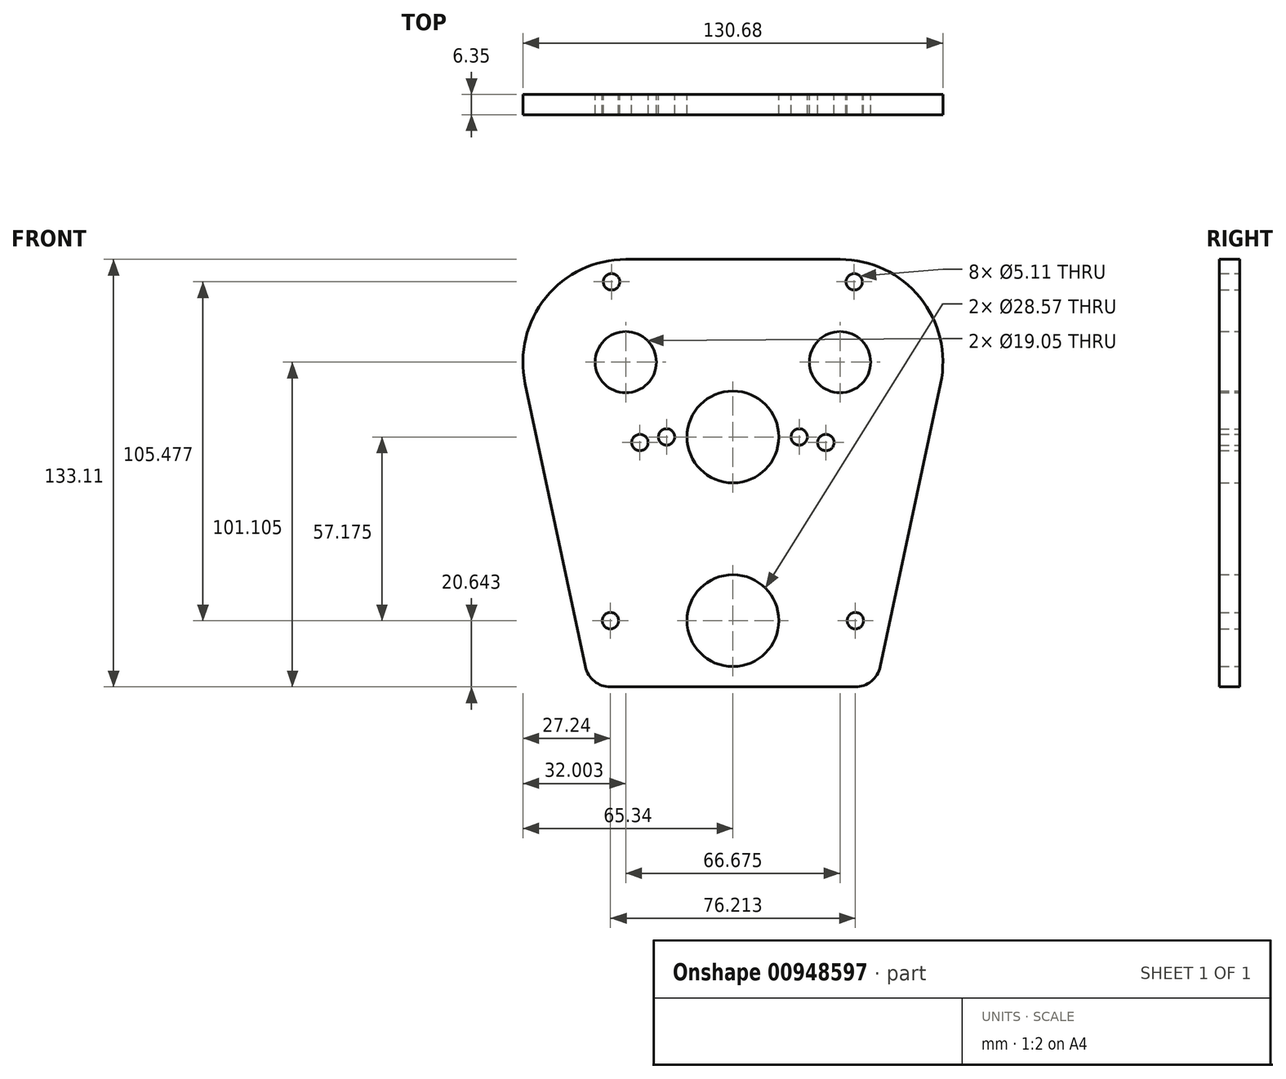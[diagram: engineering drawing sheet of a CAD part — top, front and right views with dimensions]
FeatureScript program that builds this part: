
annotation { "Feature Type Name" : "Feature", "Feature Type Description" : "" }
export const myFeature = defineFeature(function(context is Context, id is Id, definition is map)
    precondition{}
    {
        {
            var Q0;
            Q0=qCreatedBy(makeId("Front.planeOp"),FACE);
            var sketch = newSketch(context, id + "F0", { "sketchPlane" : qUnion([Q0])});
            skLineSegment(sketch, "E0.bottom", {"start": v(304.8, 23.81) * mm, "end": v(-304.8, 23.81) * mm, "construction": true});
            skLineSegment(sketch, "E0.top", {"start": v(304.8, -26.99) * mm, "end": v(-304.8, -26.99) * mm, "construction": true});
            skLineSegment(sketch, "E0.left", {"start": v(304.8, 23.81) * mm, "end": v(304.8, -26.99) * mm, "construction": true});
            skLineSegment(sketch, "E0.right", {"start": v(-304.8, 23.81) * mm, "end": v(-304.8, -26.99) * mm, "construction": true});
            skPoint(sketch, "E0.middle", {"position": v(0, -1.59) * mm});
            skCircle(sketch, "E1", {"center": v(-33.34, 78.87) * mm, "radius": 32 * mm, "construction": true});
            skCircle(sketch, "E2", {"center": v(33.34, 78.87) * mm, "radius": 32 * mm, "construction": true});
            skCircle(sketch, "E3", {"center": v(33.34, 78.87) * mm, "radius": 8.9 * mm, "construction": true});
            skCircle(sketch, "E4", {"center": v(-33.34, 78.87) * mm, "radius": 8.9 * mm, "construction": true});
            skLineSegment(sketch, "E5", {"start": v(0, -1.59) * mm, "end": v(0, 78.87) * mm, "construction": true});
            skLineSegment(sketch, "E6", {"start": v(-33.34, 78.87) * mm, "end": v(0, 78.87) * mm, "construction": true});
            skLineSegment(sketch, "E7", {"start": v(0, 78.87) * mm, "end": v(33.34, 78.87) * mm, "construction": true});
            skCircle(sketch, "E8", {"center": v(0, 55.59) * mm, "radius": 31.76 * mm, "construction": true});
            skCircle(sketch, "E9", {"center": v(0, 55.59) * mm, "radius": 19.06 * mm, "construction": true});
            skCircle(sketch, "E10", {"center": v(0, -1.59) * mm, "radius": 38.11 * mm, "construction": true});
            skCircle(sketch, "E11", {"center": v(0, -1.59) * mm, "radius": 50.8 * mm, "construction": true});
            skCircle(sketch, "E12", {"center": v(0, -1.59) * mm, "radius": 25.41 * mm, "construction": true});
            skCircle(sketch, "E13", {"center": v(-33.34, 78.87) * mm, "radius": 9.53 * mm});
            skCircle(sketch, "E14", {"center": v(33.34, 78.87) * mm, "radius": 9.53 * mm});
            skCircle(sketch, "E15", {"center": v(0, 55.59) * mm, "radius": 14.29 * mm});
            skCircle(sketch, "E16", {"center": v(0, -1.59) * mm, "radius": 14.29 * mm});
            skLineSegment(sketch, "E17", {"start": v(-28.93, 53.86) * mm, "end": v(-33.34, 78.87) * mm, "construction": true});
            skLineSegment(sketch, "E18", {"start": v(-33.34, 78.87) * mm, "end": v(-37.75, 103.89) * mm, "construction": true});
            skCircle(sketch, "E19", {"center": v(-28.93, 53.86) * mm, "radius": 2.55 * mm});
            skCircle(sketch, "E20", {"center": v(-37.75, 103.89) * mm, "radius": 2.55 * mm});
            skCircle(sketch, "E21.MirrorC", {"center": v(37.75, 103.89) * mm, "radius": 2.55 * mm});
            skLineSegment(sketch, "E22.MirrorCS", {"start": v(33.34, 78.87) * mm, "end": v(37.75, 103.89) * mm, "construction": true});
            skCircle(sketch, "E23.MirrorC", {"center": v(28.93, 53.86) * mm, "radius": 2.55 * mm});
            skLineSegment(sketch, "E24.MirrorCS", {"start": v(28.93, 53.86) * mm, "end": v(33.34, 78.87) * mm, "construction": true});
            skArc(sketch, "E25", {"start": v(-33.34, 110.88) * mm, "mid": v(-58.21, 99.01) * mm, "end": v(-64.64, 72.2) * mm});
            skCircle(sketch, "E26", {"center": v(-292.1, 11.11) * mm, "radius": 2.55 * mm, "construction": true});
            skCircle(sketch, "E27.0.1.0", {"center": v(-292.1, -14.29) * mm, "radius": 2.55 * mm, "construction": true});
            skCircle(sketch, "E27.1.0.0", {"center": v(-266.7, 11.11) * mm, "radius": 2.55 * mm, "construction": true});
            skCircle(sketch, "E27.1.1.0", {"center": v(-266.7, -14.29) * mm, "radius": 2.55 * mm, "construction": true});
            skCircle(sketch, "E27.2.0.0", {"center": v(-241.3, 11.11) * mm, "radius": 2.55 * mm, "construction": true});
            skCircle(sketch, "E27.2.1.0", {"center": v(-241.3, -14.29) * mm, "radius": 2.55 * mm, "construction": true});
            skCircle(sketch, "E27.3.0.0", {"center": v(-215.9, 11.11) * mm, "radius": 2.55 * mm, "construction": true});
            skCircle(sketch, "E27.3.1.0", {"center": v(-215.9, -14.29) * mm, "radius": 2.55 * mm, "construction": true});
            skCircle(sketch, "E27.4.0.0", {"center": v(-190.5, 11.11) * mm, "radius": 2.55 * mm, "construction": true});
            skCircle(sketch, "E27.4.1.0", {"center": v(-190.5, -14.29) * mm, "radius": 2.55 * mm, "construction": true});
            skCircle(sketch, "E27.5.0.0", {"center": v(-165.1, 11.11) * mm, "radius": 2.55 * mm, "construction": true});
            skCircle(sketch, "E27.5.1.0", {"center": v(-165.1, -14.29) * mm, "radius": 2.55 * mm, "construction": true});
            skCircle(sketch, "E27.6.0.0", {"center": v(-139.7, 11.11) * mm, "radius": 2.55 * mm, "construction": true});
            skCircle(sketch, "E27.6.1.0", {"center": v(-139.7, -14.29) * mm, "radius": 2.55 * mm, "construction": true});
            skCircle(sketch, "E27.7.0.0", {"center": v(-114.3, 11.11) * mm, "radius": 2.55 * mm, "construction": true});
            skCircle(sketch, "E27.7.1.0", {"center": v(-114.3, -14.29) * mm, "radius": 2.55 * mm, "construction": true});
            skCircle(sketch, "E27.8.0.0", {"center": v(-88.9, 11.11) * mm, "radius": 2.55 * mm, "construction": true});
            skCircle(sketch, "E27.8.1.0", {"center": v(-88.9, -14.29) * mm, "radius": 2.55 * mm, "construction": true});
            skCircle(sketch, "E27.9.0.0", {"center": v(-63.5, 11.11) * mm, "radius": 2.55 * mm, "construction": true});
            skCircle(sketch, "E27.9.1.0", {"center": v(-63.5, -14.29) * mm, "radius": 2.55 * mm, "construction": true});
            skCircle(sketch, "E27.10.0.0", {"center": v(-38.1, 11.11) * mm, "radius": 2.55 * mm, "construction": true});
            skCircle(sketch, "E27.10.1.0", {"center": v(-38.1, -14.29) * mm, "radius": 2.55 * mm, "construction": true});
            skCircle(sketch, "E27.11.0.0", {"center": v(-12.7, 11.11) * mm, "radius": 2.55 * mm, "construction": true});
            skCircle(sketch, "E27.11.1.0", {"center": v(-12.7, -14.29) * mm, "radius": 2.55 * mm, "construction": true});
            skCircle(sketch, "E27.12.0.0", {"center": v(12.7, 11.11) * mm, "radius": 2.55 * mm, "construction": true});
            skCircle(sketch, "E27.12.1.0", {"center": v(12.7, -14.29) * mm, "radius": 2.55 * mm, "construction": true});
            skCircle(sketch, "E27.13.0.0", {"center": v(38.1, 11.11) * mm, "radius": 2.55 * mm, "construction": true});
            skCircle(sketch, "E27.13.1.0", {"center": v(38.1, -14.29) * mm, "radius": 2.55 * mm, "construction": true});
            skCircle(sketch, "E27.14.0.0", {"center": v(63.5, 11.11) * mm, "radius": 2.55 * mm, "construction": true});
            skCircle(sketch, "E27.14.1.0", {"center": v(63.5, -14.29) * mm, "radius": 2.55 * mm, "construction": true});
            skCircle(sketch, "E27.15.0.0", {"center": v(88.9, 11.11) * mm, "radius": 2.55 * mm, "construction": true});
            skCircle(sketch, "E27.15.1.0", {"center": v(88.9, -14.29) * mm, "radius": 2.55 * mm, "construction": true});
            skCircle(sketch, "E27.16.0.0", {"center": v(114.3, 11.11) * mm, "radius": 2.55 * mm, "construction": true});
            skCircle(sketch, "E27.16.1.0", {"center": v(114.3, -14.29) * mm, "radius": 2.55 * mm, "construction": true});
            skCircle(sketch, "E27.17.0.0", {"center": v(139.7, 11.11) * mm, "radius": 2.55 * mm, "construction": true});
            skCircle(sketch, "E27.17.1.0", {"center": v(139.7, -14.29) * mm, "radius": 2.55 * mm, "construction": true});
            skCircle(sketch, "E27.18.0.0", {"center": v(165.1, 11.11) * mm, "radius": 2.55 * mm, "construction": true});
            skCircle(sketch, "E27.18.1.0", {"center": v(165.1, -14.29) * mm, "radius": 2.55 * mm, "construction": true});
            skCircle(sketch, "E27.19.0.0", {"center": v(190.5, 11.11) * mm, "radius": 2.55 * mm, "construction": true});
            skCircle(sketch, "E27.19.1.0", {"center": v(190.5, -14.29) * mm, "radius": 2.55 * mm, "construction": true});
            skCircle(sketch, "E27.20.0.0", {"center": v(215.9, 11.11) * mm, "radius": 2.55 * mm, "construction": true});
            skCircle(sketch, "E27.20.1.0", {"center": v(215.9, -14.29) * mm, "radius": 2.55 * mm, "construction": true});
            skCircle(sketch, "E27.21.0.0", {"center": v(241.3, 11.11) * mm, "radius": 2.55 * mm, "construction": true});
            skCircle(sketch, "E27.21.1.0", {"center": v(241.3, -14.29) * mm, "radius": 2.55 * mm, "construction": true});
            skCircle(sketch, "E27.22.0.0", {"center": v(266.7, 11.11) * mm, "radius": 2.55 * mm, "construction": true});
            skCircle(sketch, "E27.22.1.0", {"center": v(266.7, -14.29) * mm, "radius": 2.55 * mm, "construction": true});
            skCircle(sketch, "E27.23.0.0", {"center": v(292.1, 11.11) * mm, "radius": 2.55 * mm, "construction": true});
            skCircle(sketch, "E27.23.1.0", {"center": v(292.1, -14.29) * mm, "radius": 2.55 * mm, "construction": true});
            skLineSegment(sketch, "E27.direction1", {"start": v(-292.1, 11.11) * mm, "end": v(-266.7, 11.11) * mm, "construction": true});
            skLineSegment(sketch, "E27.direction2", {"start": v(-292.1, 11.11) * mm, "end": v(-292.1, -14.29) * mm, "construction": true});
            skLineSegment(sketch, "E28", {"start": v(-33.34, 110.88) * mm, "end": v(33.34, 110.88) * mm});
            skArc(sketch, "E29", {"start": v(64.64, 72.2) * mm, "mid": v(58.21, 99.01) * mm, "end": v(33.34, 110.88) * mm});
            skLineSegment(sketch, "E30", {"start": v(0, -26.99) * mm, "end": v(0, 0) * mm, "construction": true});
            skCircle(sketch, "E31", {"center": v(-38.1, -14.29) * mm, "radius": 7.94 * mm, "construction": true});
            skCircle(sketch, "E32", {"center": v(38.1, -14.29) * mm, "radius": 7.94 * mm, "construction": true});
            skLineSegment(sketch, "E33", {"start": v(-38.1, -22.23) * mm, "end": v(38.1, -22.23) * mm});
            skLineSegment(sketch, "E34", {"start": v(45.86, -15.94) * mm, "end": v(64.64, 72.2) * mm});
            skArc(sketch, "E35", {"start": v(38.1, -22.23) * mm, "mid": v(43.1, -20.46) * mm, "end": v(45.86, -15.94) * mm});
            skArc(sketch, "E36", {"start": v(-38.1, -22.23) * mm, "mid": v(-43.1, -20.46) * mm, "end": v(-45.86, -15.94) * mm});
            skLineSegment(sketch, "E37", {"start": v(-45.86, -15.94) * mm, "end": v(-64.64, 72.2) * mm});
            skCircle(sketch, "E38", {"center": v(-38.1, -1.59) * mm, "radius": 2.55 * mm});
            skLineSegment(sketch, "E39", {"start": v(-38.1, 11.11) * mm, "end": v(-38.1, -1.59) * mm, "construction": true});
            skLineSegment(sketch, "E40", {"start": v(-38.1, -1.59) * mm, "end": v(-38.1, -14.29) * mm, "construction": true});
            skCircle(sketch, "E41", {"center": v(38.11, -1.59) * mm, "radius": 2.55 * mm});
            skLineSegment(sketch, "E42", {"start": v(-20.64, 55.59) * mm, "end": v(0, 55.59) * mm, "construction": true});
            skLineSegment(sketch, "E43", {"start": v(0, 55.59) * mm, "end": v(20.64, 55.59) * mm, "construction": true});
            skCircle(sketch, "E44", {"center": v(-20.64, 55.59) * mm, "radius": 2.55 * mm});
            skCircle(sketch, "E45", {"center": v(20.64, 55.59) * mm, "radius": 2.55 * mm});
            skSolve(sketch);
        }
        {
            var Q0;
            Q0 = qSketchRegion(id + "F0", true);
            extrude(context, id + "F1", {"entities" : qUnion([Q0]), "depth" : 6.35 * mm, "offsetDistance" : 25.4 * mm});
        }
    });
